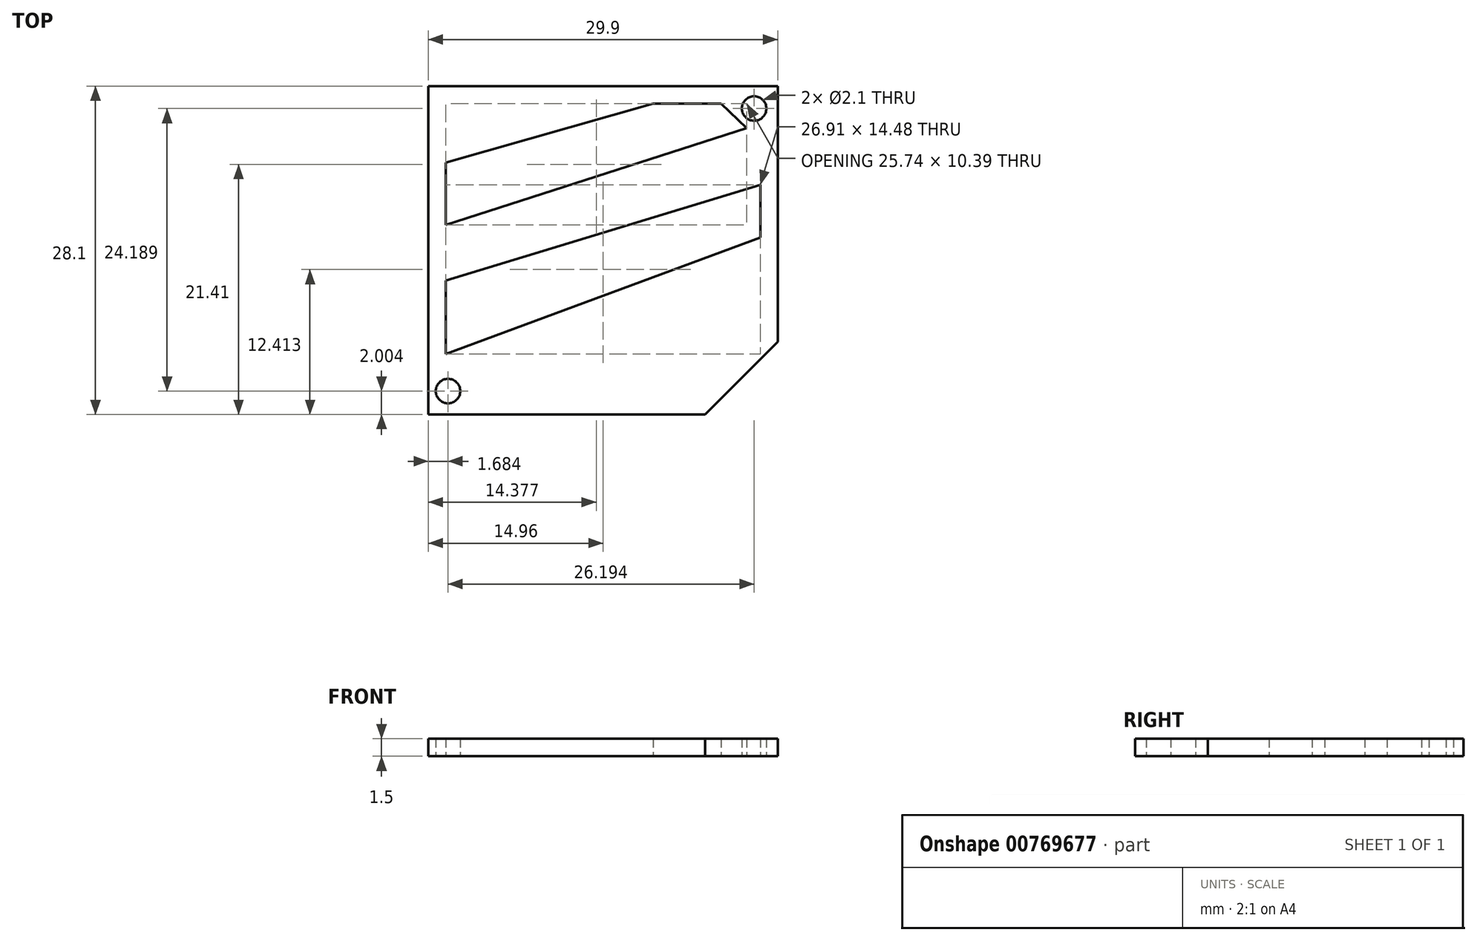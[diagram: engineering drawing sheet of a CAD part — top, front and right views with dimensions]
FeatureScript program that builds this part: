
annotation { "Feature Type Name" : "Feature", "Feature Type Description" : "" }
export const myFeature = defineFeature(function(context is Context, id is Id, definition is map)
    precondition{}
    {
        {
            var Q0;
            Q0=qCreatedBy(makeId("Top.planeOp"),FACE);
            var sketch = newSketch(context, id + "F0", { "sketchPlane" : qUnion([Q0])});
            skLineSegment(sketch, "E0", {"start": v(16.6, 15.8) * mm, "end": v(16.6, -8.19) * mm});
            skLineSegment(sketch, "E1", {"start": v(-16.3, 15.8) * mm, "end": v(16.6, 15.8) * mm});
            skLineSegment(sketch, "E2", {"start": v(-16.3, 15.8) * mm, "end": v(-16.3, -15.3) * mm});
            skLineSegment(sketch, "E3", {"start": v(-16.3, -15.3) * mm, "end": v(9.49, -15.3) * mm});
            skLineSegment(sketch, "E4", {"start": v(9.49, -15.3) * mm, "end": v(16.6, -8.19) * mm});
            skLineSegment(sketch, "E5", {"start": v(15.1, 14.3) * mm, "end": v(-14.8, 14.3) * mm});
            skLineSegment(sketch, "E6", {"start": v(-14.8, 14.3) * mm, "end": v(-14.8, -13.8) * mm});
            skLineSegment(sketch, "E7", {"start": v(-14.8, -13.8) * mm, "end": v(8.87, -13.8) * mm});
            skLineSegment(sketch, "E8", {"start": v(8.87, -13.8) * mm, "end": v(15.1, -7.57) * mm});
            skLineSegment(sketch, "E9", {"start": v(15.1, -7.57) * mm, "end": v(15.1, 14.3) * mm});
            skCircle(sketch, "E10", {"center": v(13.07, 12.4) * mm, "radius": 1.05 * mm});
            skCircle(sketch, "E11", {"center": v(-13.13, -11.8) * mm, "radius": 1.05 * mm});
            skLineSegment(sketch, "E12", {"start": v(-13.3, 12.8) * mm, "end": v(-13.3, -8.63) * mm});
            skLineSegment(sketch, "E13", {"start": v(13.6, -6.88) * mm, "end": v(13.6, 9.6) * mm});
            skLineSegment(sketch, "E14", {"start": v(13.6, -6.88) * mm, "end": v(8.15, -12.34) * mm});
            skLineSegment(sketch, "E15", {"start": v(8.15, -12.34) * mm, "end": v(-10.2, -12.34) * mm});
            skLineSegment(sketch, "E16", {"start": v(-10.2, -12.34) * mm, "end": v(-13.3, -8.63) * mm});
            skLineSegment(sketch, "E17", {"start": v(-13.3, 12.8) * mm, "end": v(10.25, 12.8) * mm});
            skLineSegment(sketch, "E18", {"start": v(10.25, 12.8) * mm, "end": v(13.6, 9.6) * mm});
            skLineSegment(sketch, "E19", {"start": v(-13.3, -6.88) * mm, "end": v(-13.3, -2.34) * mm});
            skLineSegment(sketch, "E20", {"start": v(13.6, -2.34) * mm, "end": v(13.6, 2.42) * mm});
            skLineSegment(sketch, "E21", {"start": v(-13.3, 2.42) * mm, "end": v(-13.3, 7.76) * mm});
            skLineSegment(sketch, "E22", {"start": v(13.6, -4.06) * mm, "end": v(-10.2, -12.34) * mm});
            skLineSegment(sketch, "E23", {"start": v(13.6, 1.36) * mm, "end": v(-13.3, -8.63) * mm});
            skLineSegment(sketch, "E24", {"start": v(13.6, 5.86) * mm, "end": v(-13.3, -2.34) * mm});
            skLineSegment(sketch, "E25", {"start": v(-13.3, 2.42) * mm, "end": v(12.44, 10.72) * mm});
            skLineSegment(sketch, "E26", {"start": v(4.45, 12.8) * mm, "end": v(-13.3, 7.76) * mm});
            skLineSegment(sketch, "E27", {"start": v(-13.3, 7.76) * mm, "end": v(-7.47, 12.8) * mm});
            skSolve(sketch);
        }
        {
            var Q0;
            Q0=makeQuery(id+"F0.imprint","IMPRINT",FACE,{"disambiguationData":[TD([[makeQuery(id+"F0.imprint","IMPRINT",EDGE,{"derivedFrom":sQuery(id+"F0.wireOp",EDGE,"E5")}),1.0]])]});
            var Q1;
            {var subQ3=sQuery(id+"F0.wireOp",EDGE,"E27");Q1=makeQuery(id+"F0.imprint","IMPRINT",FACE,{"disambiguationData":[TD([[makeQuery(id+"F0.imprint","IMPRINT",EDGE,{"derivedFrom":subQ3}),1.0]])]});}
            var Q2;
            {var subQ0=sQuery(id+"F0.wireOp",EDGE,"E26");Q2=makeQuery(id+"F0.imprint","IMPRINT",FACE,{"disambiguationData":[TD([[makeQuery(id+"F0.imprint","IMPRINT",EDGE,{"derivedFrom":subQ0}),-1.0]])]});}
            var Q3;
            Q3=makeQuery(id+"F0.imprint","IMPRINT",FACE,{"disambiguationData":[TD([[makeQuery(id+"F0.imprint","IMPRINT",EDGE,{"derivedFrom":sQuery(id+"F0.wireOp",EDGE,"E21")}),-1.0]])]});
            var Q4;
            {var subQ4=sQuery(id+"F0.wireOp",EDGE,"E24");Q4=makeQuery(id+"F0.imprint","IMPRINT",FACE,{"disambiguationData":[TD([[makeQuery(id+"F0.imprint","IMPRINT",EDGE,{"derivedFrom":subQ4}),-1.0]])]});}
            var Q5;
            {var subQ0=sQuery(id+"F0.wireOp",EDGE,"E19");Q5=makeQuery(id+"F0.imprint","IMPRINT",FACE,{"disambiguationData":[TD([[makeQuery(id+"F0.imprint","IMPRINT",EDGE,{"derivedFrom":subQ0}),-1.0]])]});}
            var Q6;
            Q6=makeQuery(id+"F0.imprint","IMPRINT",FACE,{"disambiguationData":[TD([[makeQuery(id+"F0.imprint","IMPRINT",EDGE,{"derivedFrom":sQuery(id+"F0.wireOp",EDGE,"E16")}),-1.0]])]});
            var Q7;
            {var subQ0=sQuery(id+"F0.wireOp",EDGE,"E14");Q7=makeQuery(id+"F0.imprint","IMPRINT",FACE,{"disambiguationData":[TD([[makeQuery(id+"F0.imprint","IMPRINT",EDGE,{"derivedFrom":subQ0}),-1.0]])]});}
            extrude(context, id + "F1", {"entities" : qUnion([Q0, Q1, Q2, Q3, Q4, Q5, Q6, Q7]), "depth" : 1.5 * mm, "offsetDistance" : 25 * mm});
        }
    });
